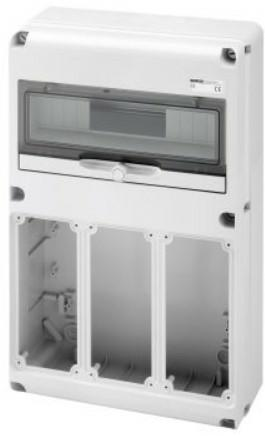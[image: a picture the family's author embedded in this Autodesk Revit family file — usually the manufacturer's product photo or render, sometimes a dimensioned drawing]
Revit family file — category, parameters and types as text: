
# Revit family: Building-IEC309Boards-GEWISS-68QDIN-DISTRIBUTION-BOARD-14MOD_3SOCKET-OUTLETS_IB_VERT
name_source: partatom
category: Apparecchi elettrici
units: mm (PartAtom-declared; Revit-internal decimal feet)

## family parameters
Condiviso = No
Host = Superficie
Mantenere orientamento annotazione = Sì
Punto di calcolo locali = Sì
Quota connettore circolare = Usa diametro
Taglio con vuoti quando caricato = No
Tipo di parte = Normale

## types (1)
- GW68010N - Q-DIN 14M 3 FLANGES S.O.BL.VR.SBF IP65
    Accordance with Standards = EN 60208 - EN 60670-1 - IEC 60670-24
    Catalogue = BUILDING
    Catalogue Range = 68 QDIN
    Colour = Grey RAL 7035
    Descrizione = Q-DIN 14M 3 FLANGES S.O.BL.VR.SBF IP65
    Dispersible power A (W) = 24
    Dispersible power B (W) = 64
    EAN code = 8011564744813
    Electrocod = 2242
    Glow Wire Test = 650°C
    Houseable interloc. socket. = 3 IB Vert. 16/32A IP67
    Houseable socket = 3 IB Vert. 16/32A IP67
    IDF = a79db918-e74e-4eae-8f25-ec0c9aa4b606
    IDT = b7fa234f-6082-4e77-ab12-b88f512de078
    IP degree = IP65
    Immagine tipo = GW68010N.jpg
    Installation type = Surface-mounting
    Insulation class = II
    L_Moduli = 266 mm  [stored 0.872703 ft]
    Modello = GW68010N
    N_Moduli = 14 mm  [stored 0.0459318 ft]
    No. IB socket-outlets houseable = 3 IB Vert. 16/32A IP67
    No. of blank lids supplied = 1 IB 16/32A
    No. of modules EN 50022 = 14
    No. of provided blank lids = 1 IB 16/32A
    Operating temperature: = -25 +40 °C
    POMELLO = bianco
    PRESA = rosso
    Produttore = GEWISS S.p.A.
    Prospetto di default = 1219 mm
    SEO = Board
    STRUTTURA = RAL - 7035
    STRUTTURA ALTA = Poche
    Shock resistance = IK08
    Spostamento_S = 1000 mm  [stored 3.28084 ft]
    Technical sheet = https://www.gewiss.com
    Thermo-pressure with ball = 70
    URL = https://www.gewiss.com
    VETRO = Vetro
    Version file RFA = 21.5
    Version type = Empty
    Working temperature = -25 ÷ +40 °C

note: source unit labels omitted for Thermo-pressure with ball — the stored unit's dimension contradicts the parameter name (converter mislabeling)

note: [stored X ft] marks values corroborated as IEEE doubles in the binary element streams (Revit-internal decimal feet)

## geometry (parser evidence)
native form markers: Sweep x5
no freeform markers — native parametric forms only
